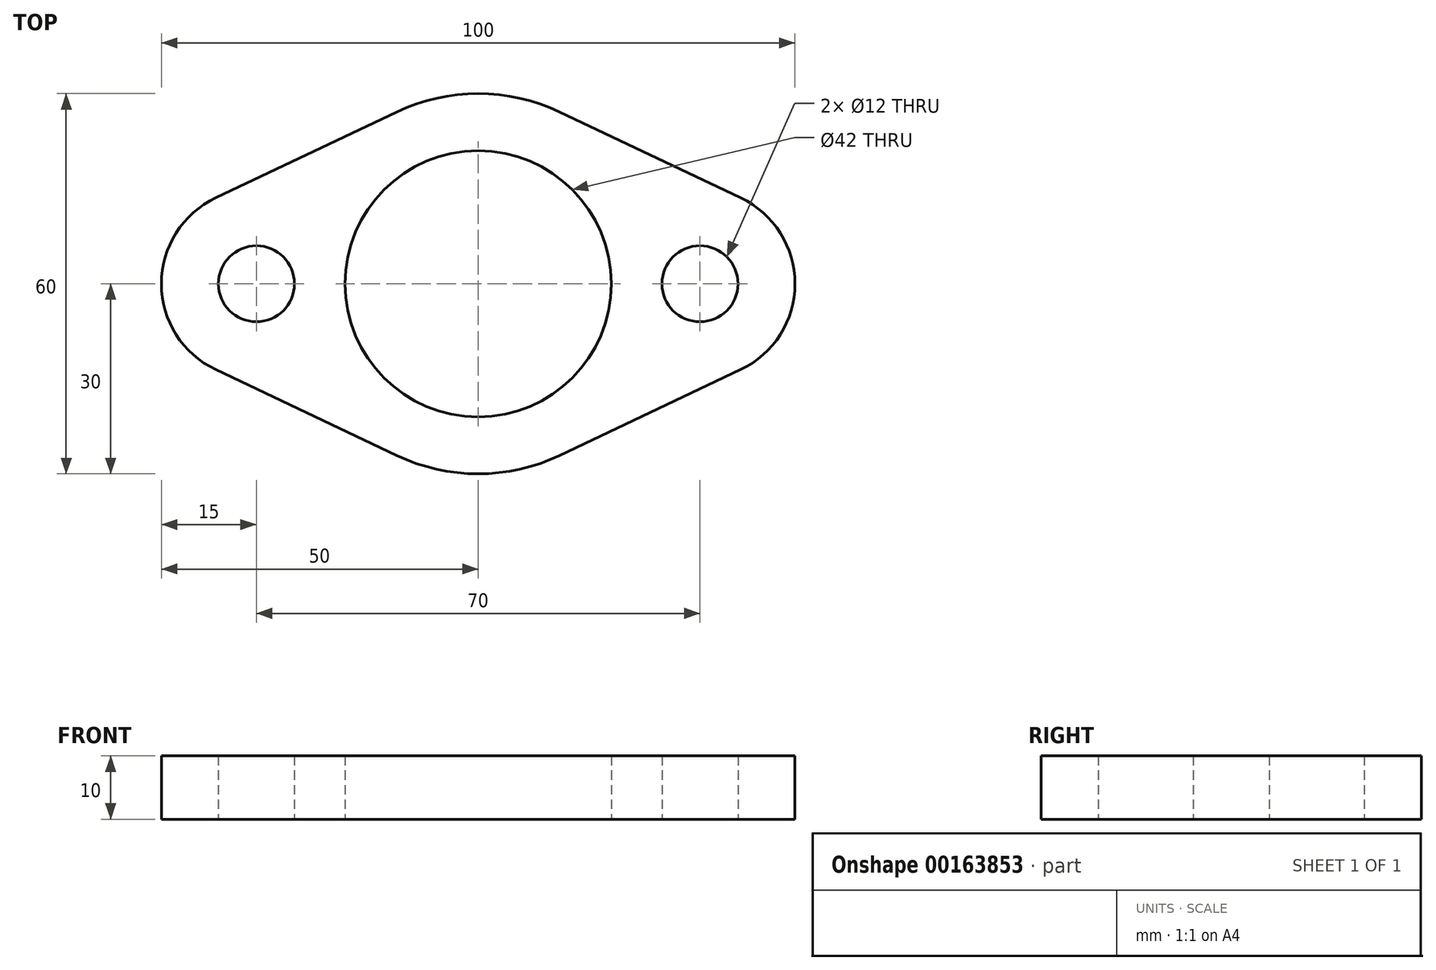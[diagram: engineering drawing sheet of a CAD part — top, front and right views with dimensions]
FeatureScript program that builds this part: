
annotation { "Feature Type Name" : "Feature", "Feature Type Description" : "" }
export const myFeature = defineFeature(function(context is Context, id is Id, definition is map)
    precondition{}
    {
        {
            var Q0;
            Q0=qCreatedBy(makeId("Top.planeOp"),FACE);
            var sketch = newSketch(context, id + "F0", { "sketchPlane" : qUnion([Q0])});
            skArc(sketch, "E0", {"start": v(21, 0) * mm, "mid": v(14.85, 14.85) * mm, "end": v(0, 21) * mm});
            skArc(sketch, "E1", {"start": v(12.86, 27.1) * mm, "mid": v(6.59, 29.27) * mm, "end": v(0, 30) * mm});
            skArc(sketch, "E2", {"start": v(41, 0) * mm, "mid": v(35, 6) * mm, "end": v(29, 0) * mm});
            skArc(sketch, "E3", {"start": v(50, 0) * mm, "mid": v(47.68, 8.02) * mm, "end": v(41.43, 13.55) * mm});
            skLineSegment(sketch, "E4", {"start": v(35, 0) * mm, "end": v(35, 30.53) * mm, "construction": true});
            skLineSegment(sketch, "E5", {"start": v(12.86, 27.1) * mm, "end": v(41.43, 13.55) * mm});
            skLineSegment(sketch, "E6", {"start": v(-48.99, 0) * mm, "end": v(57.93, 0) * mm, "construction": true});
            skLineSegment(sketch, "E7", {"start": v(0, 39.76) * mm, "end": v(0, -39.1) * mm, "construction": true});
            skArc(sketch, "E8.MirrorCS", {"start": v(-12.86, 27.1) * mm, "mid": v(-6.59, 29.27) * mm, "end": v(0, 30) * mm});
            skLineSegment(sketch, "E9.MirrorCS", {"start": v(-12.86, 27.1) * mm, "end": v(-41.43, 13.55) * mm});
            skArc(sketch, "E10.MirrorCS", {"start": v(-50, 0) * mm, "mid": v(-47.68, 8.02) * mm, "end": v(-41.43, 13.55) * mm});
            skArc(sketch, "E11.MirrorCS", {"start": v(-41, 0) * mm, "mid": v(-35, 6) * mm, "end": v(-29, 0) * mm});
            skArc(sketch, "E12.MirrorCS", {"start": v(-21, 0) * mm, "mid": v(-14.85, 14.85) * mm, "end": v(0, 21) * mm});
            skLineSegment(sketch, "E13.MirrorCS", {"start": v(48.99, 0) * mm, "end": v(-57.93, 0) * mm, "construction": true});
            skArc(sketch, "E14.MirrorCS", {"start": v(21, 0) * mm, "mid": v(14.85, -14.85) * mm, "end": v(0, -21) * mm});
            skArc(sketch, "E15.MirrorCS", {"start": v(-21, 0) * mm, "mid": v(-14.85, -14.85) * mm, "end": v(0, -21) * mm});
            skArc(sketch, "E16.MirrorCS", {"start": v(-41, 0) * mm, "mid": v(-35, -6) * mm, "end": v(-29, 0) * mm});
            skArc(sketch, "E17.MirrorCS", {"start": v(-50, 0) * mm, "mid": v(-47.68, -8.02) * mm, "end": v(-41.43, -13.55) * mm});
            skLineSegment(sketch, "E18.MirrorCS", {"start": v(-12.86, -27.1) * mm, "end": v(-41.43, -13.55) * mm});
            skArc(sketch, "E19.MirrorCS", {"start": v(-12.86, -27.1) * mm, "mid": v(-6.59, -29.27) * mm, "end": v(0, -30) * mm});
            skArc(sketch, "E20.MirrorCS", {"start": v(12.86, -27.1) * mm, "mid": v(6.59, -29.27) * mm, "end": v(0, -30) * mm});
            skLineSegment(sketch, "E21.MirrorCS", {"start": v(12.86, -27.1) * mm, "end": v(41.43, -13.55) * mm});
            skArc(sketch, "E22.MirrorCS", {"start": v(50, 0) * mm, "mid": v(47.68, -8.02) * mm, "end": v(41.43, -13.55) * mm});
            skArc(sketch, "E23.MirrorCS", {"start": v(41, 0) * mm, "mid": v(35, -6) * mm, "end": v(29, 0) * mm});
            skSolve(sketch);
        }
        {
            var Q0;
            Q0=makeQuery(id+"F0.imprint","IMPRINT",FACE,{"disambiguationData":[TD([[makeQuery(id+"F0.imprint","IMPRINT",EDGE,{"derivedFrom":sQuery(id+"F0.wireOp",EDGE,"E0")}),-1.0]])]});
            extrude(context, id + "F1", {"entities" : qUnion([Q0]), "depth" : 10 * mm});
        }
    });
